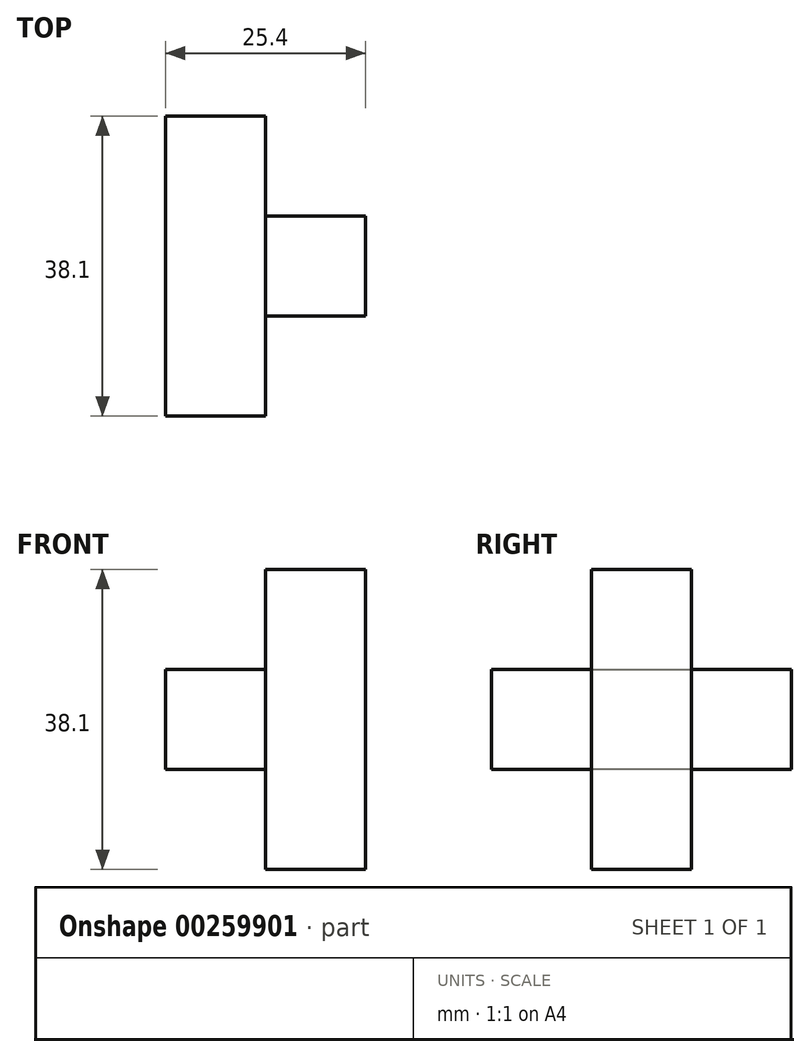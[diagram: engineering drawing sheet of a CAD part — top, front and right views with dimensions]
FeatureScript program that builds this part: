
annotation { "Feature Type Name" : "Feature", "Feature Type Description" : "" }
export const myFeature = defineFeature(function(context is Context, id is Id, definition is map)
    precondition{}
    {
        {
            var Q0;
            Q0=qCreatedBy(makeId("Right.planeOp"),FACE);
            var sketch = newSketch(context, id + "F0", { "sketchPlane" : qUnion([Q0])});
            skLineSegment(sketch, "E0", {"start": v(0, 0) * mm, "end": v(0, 38.1) * mm});
            skLineSegment(sketch, "E1", {"start": v(0, 38.1) * mm, "end": v(12.7, 38.1) * mm});
            skLineSegment(sketch, "E2", {"start": v(12.7, 38.1) * mm, "end": v(12.7, 0) * mm});
            skLineSegment(sketch, "E3", {"start": v(12.7, 0) * mm, "end": v(0, 0) * mm});
            skSolve(sketch);
        }
        {
            var Q0;
            Q0=makeQuery(id+"F0.imprint","IMPRINT",FACE,{"disambiguationData":[TD([[makeQuery(id+"F0.imprint","IMPRINT",EDGE,{"derivedFrom":sQuery(id+"F0.wireOp",EDGE,"E0")}),-1.0]])]});
            extrude(context, id + "F1", {"entities" : qUnion([Q0]), "depth" : 12.7 * mm});
        }
        {
            var Q0;
            Q0=qCreatedBy(makeId("Right.planeOp"),FACE);
            var sketch = newSketch(context, id + "F2", { "sketchPlane" : qUnion([Q0])});
            skLineSegment(sketch, "E4", {"start": v(0, 0) * mm, "end": v(0, 12.7) * mm});
            skLineSegment(sketch, "E5", {"start": v(0, 12.7) * mm, "end": v(-12.7, 12.7) * mm});
            skLineSegment(sketch, "E6", {"start": v(-12.7, 12.7) * mm, "end": v(25.4, 12.7) * mm});
            skLineSegment(sketch, "E7", {"start": v(-12.7, 12.7) * mm, "end": v(-12.7, 25.4) * mm});
            skLineSegment(sketch, "E8", {"start": v(-12.7, 25.4) * mm, "end": v(25.4, 25.4) * mm});
            skLineSegment(sketch, "E9", {"start": v(25.4, 25.4) * mm, "end": v(25.4, 12.7) * mm});
            skSolve(sketch);
        }
        {
            var Q0;
            {var subQ0=sQuery(id+"F2.wireOp",EDGE,"E7");Q0=makeQuery(id+"F2.imprint","IMPRINT",FACE,{"disambiguationData":[TD([[makeQuery(id+"F2.imprint","IMPRINT",EDGE,{"derivedFrom":subQ0}),-1.0]])]});}
            extrude(context, id + "F3", {"entities" : qUnion([Q0]), "operationType" : NewBodyOperationType.ADD, "oppositeDirection" : true, "depth" : 12.7 * mm});
        }
    });
